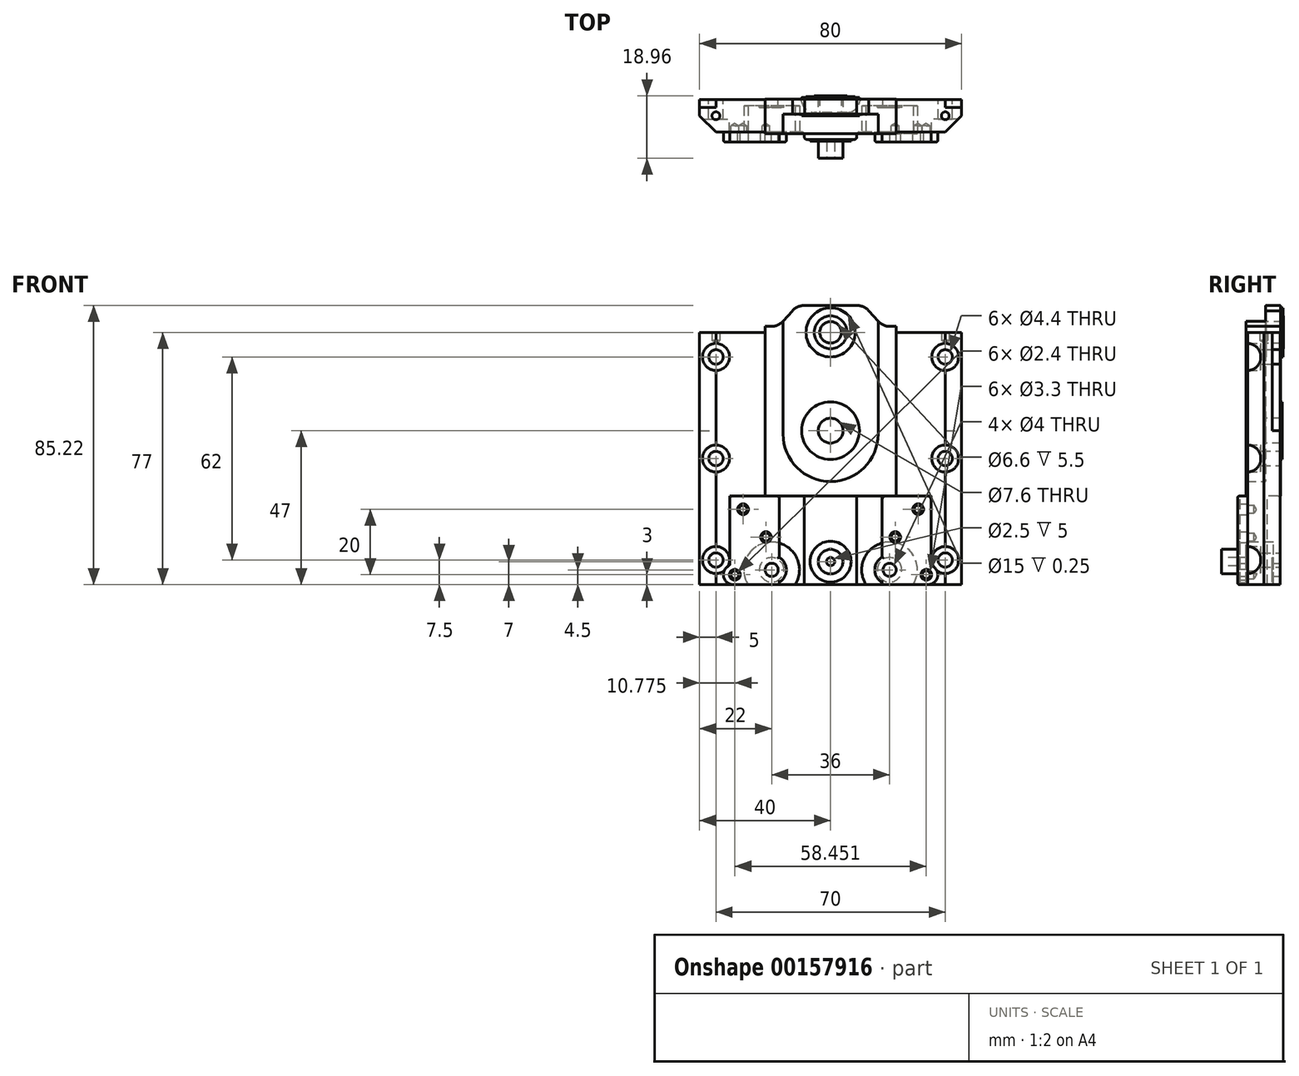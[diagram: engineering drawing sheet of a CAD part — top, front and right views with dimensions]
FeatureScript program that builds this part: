
annotation { "Feature Type Name" : "Feature", "Feature Type Description" : "" }
export const myFeature = defineFeature(function(context is Context, id is Id, definition is map)
    precondition{}
    {
        {
            var Q0;
            Q0=qCreatedBy(makeId("Front.planeOp"),FACE);
            var sketch = newSketch(context, id + "F0", { "sketchPlane" : qUnion([Q0])});
            skArc(sketch, "E0.MirrorCS", {"start": v(7.93, 38.21) * mm, "mid": v(9.99, 37.84) * mm, "end": v(11.66, 36.57) * mm});
            skArc(sketch, "E1.MirrorCS", {"start": v(18.2, 31.8) * mm, "mid": v(16.18, 32.23) * mm, "end": v(14.5, 33.43) * mm});
            skLineSegment(sketch, "E2.MirrorCS", {"start": v(20, -20) * mm, "end": v(20, 31.8) * mm});
            skLineSegment(sketch, "E3", {"start": v(20, 31.8) * mm, "end": v(18.2, 31.8) * mm});
            skLineSegment(sketch, "E4", {"start": v(11.66, 36.57) * mm, "end": v(14.5, 33.43) * mm});
            skCircle(sketch, "E5", {"center": v(0, 0) * mm, "radius": 3.8 * mm});
            skLineSegment(sketch, "E6.MirrorCS", {"start": v(-20, -20) * mm, "end": v(-20, 31.8) * mm});
            skArc(sketch, "E7.MirrorCS", {"start": v(-18.2, 31.8) * mm, "mid": v(-16.18, 32.23) * mm, "end": v(-14.5, 33.43) * mm});
            skLineSegment(sketch, "E8.MirrorCS", {"start": v(-11.66, 36.57) * mm, "end": v(-14.5, 33.43) * mm});
            skArc(sketch, "E9.MirrorCS", {"start": v(-7.93, 38.21) * mm, "mid": v(-9.99, 37.84) * mm, "end": v(-11.66, 36.57) * mm});
            skLineSegment(sketch, "E10", {"start": v(-18.2, 31.8) * mm, "end": v(-20, 31.8) * mm});
            skLineSegment(sketch, "E11", {"start": v(-20, -20) * mm, "end": v(20, -20) * mm});
            skLineSegment(sketch, "E12", {"start": v(-7.93, 38.21) * mm, "end": v(7.93, 38.21) * mm});
            skSolve(sketch);
        }
        {
            var Q0;
            Q0 = qSketchRegion(id + "F0", true);
            extrude(context, id + "F1", {"entities" : qUnion([Q0]), "oppositeDirection" : true, "depth" : 4.5 * mm});
        }
        {
            var Q0;
            Q0=makeQuery(id+"F1.opExtrude","CAP_FACE",FACE,{"disambiguationData":[OSD([sQuery(id+"F0.wireOp",EDGE,"7c40d91c-51bf-44e0-baa0-2f148f85da3b.MirrorCS"),sQuery(id+"F0.wireOp",EDGE,"E0.MirrorCS"),sQuery(id+"F0.wireOp",EDGE,"E1.MirrorCS"),sQuery(id+"F0.wireOp",EDGE,"E2.MirrorCS"),sQuery(id+"F0.wireOp",EDGE,"E3"),sQuery(id+"F0.wireOp",EDGE,"ZX2brBpr-0A55-FfDv-xvMl-bLhvxCoY3JhF"),sQuery(id+"F0.wireOp",EDGE,"E4"),sQuery(id+"F0.wireOp",EDGE,"E5"),sQuery(id+"F0.wireOp",EDGE,"f4add119-3c6b-4ee7-8744-91418914288d0.MirrorCS"),sQuery(id+"F0.wireOp",EDGE,"E6.MirrorCS"),sQuery(id+"F0.wireOp",EDGE,"E7.MirrorCS"),sQuery(id+"F0.wireOp",EDGE,"E8.MirrorCS"),sQuery(id+"F0.wireOp",EDGE,"2a2e974d-f992-448b-8597-4e99c86357490.MirrorCS"),sQuery(id+"F0.wireOp",EDGE,"E9.MirrorCS"),sQuery(id+"F0.wireOp",EDGE,"E10")])],"isStart":true});
            var sketch = newSketch(context, id + "F2", { "sketchPlane" : qUnion([Q0])});
            skPoint(sketch, "E13.orphan", {"position": v(9.9, 31.39) * mm});
            skLineSegment(sketch, "E14.0", {"start": v(20, -20) * mm, "end": v(20, 31.8) * mm});
            skLineSegment(sketch, "E15.0", {"start": v(20, -20) * mm, "end": v(-20, -20) * mm});
            skLineSegment(sketch, "E16.0", {"start": v(-20, -20) * mm, "end": v(-20, 31.8) * mm});
            skLineSegment(sketch, "E17.0", {"start": v(-18.2, 31.8) * mm, "end": v(-20, 31.8) * mm});
            skLineSegment(sketch, "E18.0", {"start": v(20, 31.8) * mm, "end": v(18.2, 31.8) * mm});
            skArc(sketch, "E19.0", {"start": v(18.2, 31.8) * mm, "mid": v(16.18, 32.23) * mm, "end": v(14.5, 33.43) * mm});
            skArc(sketch, "E20.0", {"start": v(-18.2, 31.8) * mm, "mid": v(-16.18, 32.23) * mm, "end": v(-14.5, 33.43) * mm});
            skLineSegment(sketch, "E21", {"start": v(-14.5, 33.43) * mm, "end": v(-14.5, -1.03) * mm});
            skLineSegment(sketch, "E22", {"start": v(14.5, 33.43) * mm, "end": v(14.5, -1.03) * mm});
            skArc(sketch, "E23", {"start": v(-14.5, -1.03) * mm, "mid": v(0, -15.54) * mm, "end": v(14.5, -1.03) * mm});
            skSolve(sketch);
        }
        {
            var Q0;
            Q0 = qSketchRegion(id + "F2", true);
            extrude(context, id + "F3", {"entities" : qUnion([Q0]), "operationType" : NewBodyOperationType.ADD, "depth" : 6 * mm});
        }
        {
            var Q0;
            Q0=makeQuery(id+"F3.boolean.opBoolean","MERGE",FACE,{"derivedFrom":[makeQuery(id+"F1.opExtrude","SWEPT_FACE",FACE,{"disambiguationData":[OSD([sQuery(id+"F0.wireOp",EDGE,"ZX2brBpr-0A55-FfDv-xvMl-bLhvxCoY3JhF"),sQuery(id+"F0.wireOp",EDGE,"f4add119-3c6b-4ee7-8744-91418914288d0.MirrorCS")])]}),makeQuery(id+"F3.opExtrude","SWEPT_FACE",FACE,{"disambiguationData":[OSD([sQuery(id+"F2.wireOp",EDGE,"E15.0")])]})]});
            var sketch = newSketch(context, id + "F4", { "sketchPlane" : qUnion([Q0])});
            skLineSegment(sketch, "E24.0", {"start": v(5, -0.5) * mm, "end": v(-5, -0.5) * mm});
            skPoint(sketch, "E25.visualSharp", {"position": v(10.82, 7.76) * mm});
            skPoint(sketch, "E26.visualSharp", {"position": v(-11.68, 7.76) * mm});
            skArc(sketch, "E27", {"start": v(5, -0.5) * mm, "mid": v(7.56, -1.45) * mm, "end": v(8.9, -3.83) * mm});
            skArc(sketch, "E28", {"start": v(-5, -0.5) * mm, "mid": v(-7.56, -1.45) * mm, "end": v(-8.9, -3.83) * mm});
            skLineSegment(sketch, "E29", {"start": v(-7.25, 7.76) * mm, "end": v(7.25, 7.76) * mm});
            skLineSegment(sketch, "E30", {"start": v(-8, 7) * mm, "end": v(-8, 6.3) * mm});
            skLineSegment(sketch, "E31", {"start": v(8, 7) * mm, "end": v(8, 6.3) * mm});
            skPoint(sketch, "E32.visualSharp", {"position": v(-8, 7.76) * mm});
            skArc(sketch, "E32.filletArc", {"start": v(-7.25, 7.76) * mm, "mid": v(-7.78, 7.54) * mm, "end": v(-8, 7) * mm});
            skPoint(sketch, "E33.visualSharp", {"position": v(8, 7.76) * mm});
            skArc(sketch, "E33.filletArc", {"start": v(8, 7) * mm, "mid": v(7.78, 7.54) * mm, "end": v(7.25, 7.76) * mm});
            skPoint(sketch, "E34.visualSharp", {"position": v(-8, 5.54) * mm});
            skArc(sketch, "E34.filletArc", {"start": v(-8.75, 5.54) * mm, "mid": v(-8.22, 5.76) * mm, "end": v(-8, 6.3) * mm});
            skPoint(sketch, "E35.visualSharp", {"position": v(8, 5.54) * mm});
            skArc(sketch, "E35.filletArc", {"start": v(8, 6.3) * mm, "mid": v(8.22, 5.76) * mm, "end": v(8.75, 5.54) * mm});
            skPoint(sketch, "E36.visualSharp", {"position": v(-8.96, -4.46) * mm});
            skArc(sketch, "E36.filletArc", {"start": v(-9.65, -4.46) * mm, "mid": v(-9.16, -4.28) * mm, "end": v(-8.9, -3.83) * mm});
            skPoint(sketch, "E37.visualSharp", {"position": v(8.96, -4.46) * mm});
            skArc(sketch, "E37.filletArc", {"start": v(8.9, -3.83) * mm, "mid": v(9.16, -4.28) * mm, "end": v(9.65, -4.46) * mm});
            skLineSegment(sketch, "E38", {"start": v(40, -4.46) * mm, "end": v(40, 2.2) * mm});
            skLineSegment(sketch, "E39.MirrorCS", {"start": v(-40, -4.46) * mm, "end": v(-40, 2.2) * mm});
            skLineSegment(sketch, "E40", {"start": v(-9.65, -4.46) * mm, "end": v(-40, -4.46) * mm});
            skLineSegment(sketch, "E41", {"start": v(9.65, -4.46) * mm, "end": v(40, -4.46) * mm});
            skLineSegment(sketch, "E42", {"start": v(8.75, 5.54) * mm, "end": v(26.88, 5.54) * mm});
            skLineSegment(sketch, "E43", {"start": v(-8.75, 5.54) * mm, "end": v(-26.88, 5.54) * mm});
            skLineSegment(sketch, "E44", {"start": v(26.88, 5.54) * mm, "end": v(40, 5.54) * mm});
            skLineSegment(sketch, "E45", {"start": v(40, 5.54) * mm, "end": v(40, 2.2) * mm});
            skLineSegment(sketch, "E46", {"start": v(-26.88, 5.54) * mm, "end": v(-40, 5.54) * mm});
            skLineSegment(sketch, "E47", {"start": v(-40, 5.54) * mm, "end": v(-40, 2.2) * mm});
            skSolve(sketch);
        }
        {
            var Q0;
            Q0 = qSketchRegion(id + "F4", true);
            extrude(context, id + "F5", {"entities" : qUnion([Q0]), "operationType" : NewBodyOperationType.ADD, "depth" : 27 * mm});
        }
        {
            var Q0;
            Q0=makeQuery(id+"F1.opExtrude","CAP_FACE",FACE,{"disambiguationData":[OSD([sQuery(id+"F0.wireOp",EDGE,"7c40d91c-51bf-44e0-baa0-2f148f85da3b.MirrorCS"),sQuery(id+"F0.wireOp",EDGE,"E0.MirrorCS"),sQuery(id+"F0.wireOp",EDGE,"E1.MirrorCS"),sQuery(id+"F0.wireOp",EDGE,"E2.MirrorCS"),sQuery(id+"F0.wireOp",EDGE,"E3"),sQuery(id+"F0.wireOp",EDGE,"ZX2brBpr-0A55-FfDv-xvMl-bLhvxCoY3JhF"),sQuery(id+"F0.wireOp",EDGE,"E4"),sQuery(id+"F0.wireOp",EDGE,"E5"),sQuery(id+"F0.wireOp",EDGE,"f4add119-3c6b-4ee7-8744-91418914288d0.MirrorCS"),sQuery(id+"F0.wireOp",EDGE,"E6.MirrorCS"),sQuery(id+"F0.wireOp",EDGE,"E7.MirrorCS"),sQuery(id+"F0.wireOp",EDGE,"E8.MirrorCS"),sQuery(id+"F0.wireOp",EDGE,"2a2e974d-f992-448b-8597-4e99c86357490.MirrorCS"),sQuery(id+"F0.wireOp",EDGE,"E9.MirrorCS"),sQuery(id+"F0.wireOp",EDGE,"E10")])],"isStart":true});
            var sketch = newSketch(context, id + "F6", { "sketchPlane" : qUnion([Q0])});
            skCircle(sketch, "E48.0", {"center": v(0, 0) * mm, "radius": 3.8 * mm});
            skCircle(sketch, "E49.0", {"center": v(0, 0) * mm, "radius": 8.8 * mm});
            skSolve(sketch);
        }
        {
            var Q0;
            Q0 = qSketchRegion(id + "F6", true);
            extrude(context, id + "F7", {"entities" : qUnion([Q0]), "operationType" : NewBodyOperationType.ADD, "depth" : 0.5 * mm});
        }
        {
            var Q0;
            Q0=makeQuery(id+"F1.opExtrude","CAP_FACE",FACE,{"disambiguationData":[OSD([sQuery(id+"F0.wireOp",EDGE,"7c40d91c-51bf-44e0-baa0-2f148f85da3b.MirrorCS"),sQuery(id+"F0.wireOp",EDGE,"E0.MirrorCS"),sQuery(id+"F0.wireOp",EDGE,"E1.MirrorCS"),sQuery(id+"F0.wireOp",EDGE,"E2.MirrorCS"),sQuery(id+"F0.wireOp",EDGE,"E3"),sQuery(id+"F0.wireOp",EDGE,"ZX2brBpr-0A55-FfDv-xvMl-bLhvxCoY3JhF"),sQuery(id+"F0.wireOp",EDGE,"E4"),sQuery(id+"F0.wireOp",EDGE,"E5"),sQuery(id+"F0.wireOp",EDGE,"f4add119-3c6b-4ee7-8744-91418914288d0.MirrorCS"),sQuery(id+"F0.wireOp",EDGE,"E6.MirrorCS"),sQuery(id+"F0.wireOp",EDGE,"E7.MirrorCS"),sQuery(id+"F0.wireOp",EDGE,"E8.MirrorCS"),sQuery(id+"F0.wireOp",EDGE,"2a2e974d-f992-448b-8597-4e99c86357490.MirrorCS"),sQuery(id+"F0.wireOp",EDGE,"E9.MirrorCS"),sQuery(id+"F0.wireOp",EDGE,"E10")])],"isStart":false});
            var sketch = newSketch(context, id + "F8", { "sketchPlane" : qUnion([Q0])});
            skCircle(sketch, "E50.0", {"center": v(0, 0) * mm, "radius": 3.8 * mm});
            skCircle(sketch, "E51.0", {"center": v(0, 0) * mm, "radius": 8.8 * mm});
            skSolve(sketch);
        }
        {
            var Q0;
            Q0 = qSketchRegion(id + "F8", true);
            extrude(context, id + "F9", {"entities" : qUnion([Q0]), "operationType" : NewBodyOperationType.ADD, "depth" : 0.55 * mm});
        }
        {
            var Q0;
            {var subQ0=sQuery(id+"F4.wireOp",EDGE,"E45");var subQ1=sQuery(id+"F4.wireOp",EDGE,"E38");var subQ2=sQuery(id+"F4.wireOp",EDGE,"E41");var subQ3=sQuery(id+"F4.wireOp",EDGE,"E44");var subQ4=sQuery(id+"F4.wireOp",EDGE,"E42");Q0=makeQuery(id+"F5.boolean.opBoolean","SPLIT",FACE,{"disambiguationData":[TD([makeQuery(id+"F1.opExtrude","SWEPT_FACE",FACE,{"disambiguationData":[OSD([sQuery(id+"F0.wireOp",EDGE,"E2.MirrorCS")])]})])],"derivedFrom":makeQuery(id+"F5.opExtrude","CAP_FACE",FACE,{"disambiguationData":[OSD([sQuery(id+"F4.wireOp",EDGE,"E24.0"),sQuery(id+"F4.wireOp",EDGE,"E27"),sQuery(id+"F4.wireOp",EDGE,"E28"),sQuery(id+"F4.wireOp",EDGE,"E29"),sQuery(id+"F4.wireOp",EDGE,"E30"),sQuery(id+"F4.wireOp",EDGE,"E31"),sQuery(id+"F4.wireOp",EDGE,"E32.filletArc"),sQuery(id+"F4.wireOp",EDGE,"E33.filletArc"),sQuery(id+"F4.wireOp",EDGE,"E34.filletArc"),sQuery(id+"F4.wireOp",EDGE,"E35.filletArc"),sQuery(id+"F4.wireOp",EDGE,"E36.filletArc"),sQuery(id+"F4.wireOp",EDGE,"E37.filletArc"),subQ1,sQuery(id+"F4.wireOp",EDGE,"E39.MirrorCS"),sQuery(id+"F4.wireOp",EDGE,"E40"),subQ2,subQ4,sQuery(id+"F4.wireOp",EDGE,"E43"),subQ3,subQ0,sQuery(id+"F4.wireOp",EDGE,"E46"),sQuery(id+"F4.wireOp",EDGE,"E47")])],"isStart":true})});}
            var sketch = newSketch(context, id + "F10", { "sketchPlane" : qUnion([Q0])});
            skLineSegment(sketch, "E52.0", {"start": v(20, 4.46) * mm, "end": v(40, 4.46) * mm});
            skLineSegment(sketch, "E53.0", {"start": v(40, 4.46) * mm, "end": v(40, -5.54) * mm});
            skLineSegment(sketch, "E54.0", {"start": v(20, -5.54) * mm, "end": v(40, -5.54) * mm});
            skLineSegment(sketch, "E55", {"start": v(20, 4.46) * mm, "end": v(20, -5.54) * mm});
            skLineSegment(sketch, "E56.MirrorCS", {"start": v(-20, 4.46) * mm, "end": v(-40, 4.46) * mm});
            skLineSegment(sketch, "E57.MirrorCS", {"start": v(-40, 4.46) * mm, "end": v(-40, -5.54) * mm});
            skLineSegment(sketch, "E58.MirrorCS", {"start": v(-20, -5.54) * mm, "end": v(-40, -5.54) * mm});
            skLineSegment(sketch, "E59.MirrorCS", {"start": v(-20, 4.46) * mm, "end": v(-20, -5.54) * mm});
            skSolve(sketch);
        }
        {
            var Q0;
            Q0 = qSketchRegion(id + "F10", true);
            extrude(context, id + "F11", {"entities" : qUnion([Q0]), "operationType" : NewBodyOperationType.ADD, "depth" : 50 * mm});
        }
        {
            var Q0;
            Q0=makeQuery(id+"F11.boolean.opBoolean","MERGE",EDGE,{"derivedFrom":[makeQuery(id+"F5.opExtrude","SWEPT_EDGE",EDGE,{"disambiguationData":[OSD([sQuery(id+"F4.wireOp",EDGE,"E44"),sQuery(id+"F4.wireOp",EDGE,"E45")])]}),makeQuery(id+"F11.opExtrude","SWEPT_EDGE",EDGE,{"disambiguationData":[OSD([sQuery(id+"F10.wireOp",EDGE,"E53.0"),sQuery(id+"F10.wireOp",EDGE,"E54.0")])]})]});
            var Q1;
            Q1=makeQuery(id+"F11.boolean.opBoolean","MERGE",EDGE,{"derivedFrom":[makeQuery(id+"F5.opExtrude","SWEPT_EDGE",EDGE,{"disambiguationData":[OSD([sQuery(id+"F4.wireOp",EDGE,"E46"),sQuery(id+"F4.wireOp",EDGE,"E47")])]}),makeQuery(id+"F11.opExtrude","SWEPT_EDGE",EDGE,{"disambiguationData":[OSD([sQuery(id+"F10.wireOp",EDGE,"E57.MirrorCS"),sQuery(id+"F10.wireOp",EDGE,"E58.MirrorCS")])]})]});
            chamfer(context, id + "F12", {"entities" : qUnion([Q0, Q1]), "width" : 5 * mm, "tangentPropagation" : true});
        }
        {
            var Q0;
            {var subQ0=sQuery(id+"F4.wireOp",EDGE,"E29");Q0=makeQuery(id+"F9QGCB94PZabjkV_1.boolean.opBoolean","MERGE",FACE,{"derivedFrom":[makeQuery(id+"F5.opExtrude","SWEPT_FACE",FACE,{"disambiguationData":[OSD([subQ0])]}),makeQuery(id+"F9QGCB94PZabjkV_1.opExtrude","SWEPT_FACE",FACE,{"disambiguationData":[OSD([subQ0])]})]});}
            var sketch = newSketch(context, id + "F13", { "sketchPlane" : qUnion([Q0])});
            skCircle(sketch, "E60", {"center": v(0, -40) * mm, "radius": 6.25 * mm});
            skSolve(sketch);
        }
        {
            var Q0;
            Q0 = qSketchRegion(id + "F13", true);
            extrude(context, id + "F14", {"entities" : qUnion([Q0]), "operationType" : NewBodyOperationType.ADD, "depth" : 0.5 * mm});
        }
        {
            var Q0;
            Q0=makeQuery(id+"F14.opExtrude","CAP_FACE",FACE,{"disambiguationData":[OSD([sQuery(id+"F13.wireOp",EDGE,"E60")])],"isStart":false});
            var sketch = newSketch(context, id + "F15", { "sketchPlane" : qUnion([Q0])});
            skCircle(sketch, "E61", {"center": v(0, -40) * mm, "radius": 3.75 * mm});
            skSolve(sketch);
        }
        {
            var Q0;
            Q0 = qSketchRegion(id + "F15", true);
            extrude(context, id + "F16", {"entities" : qUnion([Q0]), "operationType" : NewBodyOperationType.ADD, "depth" : 5.2 * mm});
        }
        {
            var Q0;
            Q0=makeQuery(id+"F16.opExtrude","CAP_FACE",FACE,{"disambiguationData":[OSD([sQuery(id+"F15.wireOp",EDGE,"E61")])],"isStart":false});
            var sketch = newSketch(context, id + "F17", { "sketchPlane" : qUnion([Q0])});
            skCircle(sketch, "E62", {"center": v(0, -40) * mm, "radius": 1.25 * mm});
            skSolve(sketch);
        }
        {
            var Q0;
            Q0 = qSketchRegion(id + "F17", true);
            extrude(context, id + "F18", {"entities" : qUnion([Q0]), "operationType" : NewBodyOperationType.REMOVE, "oppositeDirection" : true, "depth" : 5 * mm});
        }
        {
            var Q0;
            Q0=makeQuery(id+"F11.boolean.opBoolean","MERGE",FACE,{"derivedFrom":[makeQuery(id+"F5.opExtrude","SWEPT_FACE",FACE,{"disambiguationData":[OSD([sQuery(id+"F4.wireOp",EDGE,"E42"),sQuery(id+"F4.wireOp",EDGE,"E44")])]}),makeQuery(id+"F11.opExtrude","SWEPT_FACE",FACE,{"disambiguationData":[OSD([sQuery(id+"F10.wireOp",EDGE,"E54.0")])]})]});
            var sketch = newSketch(context, id + "F19", { "sketchPlane" : qUnion([Q0])});
            skCircle(sketch, "E63", {"center": v(18, -42.5) * mm, "radius": 8.5 * mm});
            skCircle(sketch, "E64.MirrorC", {"center": v(-18, -42.5) * mm, "radius": 8.5 * mm});
            skSolve(sketch);
        }
        {
            var Q0;
            Q0 = qSketchRegion(id + "F19", true);
            extrude(context, id + "F20", {"entities" : qUnion([Q0]), "operationType" : NewBodyOperationType.REMOVE, "oppositeDirection" : true, "depth" : 8 * mm});
        }
        {
            var Q0;
            Q0=makeQuery(id+"F20.boolean.opBoolean","COPY",FACE,{"derivedFrom":makeQuery(id+"F20.opExtrude","CAP_FACE",FACE,{"disambiguationData":[OSD([sQuery(id+"F19.wireOp",EDGE,"E63")])],"isStart":false})});
            var sketch = newSketch(context, id + "F21", { "sketchPlane" : qUnion([Q0])});
            skCircle(sketch, "E65", {"center": v(18, -42.5) * mm, "radius": 2 * mm});
            skCircle(sketch, "E66", {"center": v(18, -42.5) * mm, "radius": 3.75 * mm});
            skCircle(sketch, "E67.MirrorC", {"center": v(-18, -42.5) * mm, "radius": 2 * mm});
            skCircle(sketch, "E68.MirrorC", {"center": v(-18, -42.5) * mm, "radius": 3.75 * mm});
            skSolve(sketch);
        }
        {
            var Q0;
            Q0 = qSketchRegion(id + "F21", true);
            extrude(context, id + "F22", {"entities" : qUnion([Q0]), "operationType" : NewBodyOperationType.ADD, "depth" : 0.5 * mm});
        }
        {
            var Q0;
            Q0=makeQuery(id+"F22.boolean.opBoolean","SPLIT",FACE,{"disambiguationData":[TD([makeQuery(id+"F22.opExtrude","SWEPT_FACE",FACE,{"disambiguationData":[OSD([sQuery(id+"F21.wireOp",EDGE,"E65")])]})])],"derivedFrom":makeQuery(id+"F20.boolean.opBoolean","COPY",FACE,{"derivedFrom":makeQuery(id+"F20.opExtrude","CAP_FACE",FACE,{"disambiguationData":[OSD([sQuery(id+"F19.wireOp",EDGE,"E63")])],"isStart":false})})});
            var Q1;
            Q1=makeQuery(id+"F22.boolean.opBoolean","SPLIT",FACE,{"disambiguationData":[TD([makeQuery(id+"F22.opExtrude","SWEPT_FACE",FACE,{"disambiguationData":[OSD([sQuery(id+"F21.wireOp",EDGE,"E67.MirrorC")])]})])],"derivedFrom":makeQuery(id+"F20.boolean.opBoolean","COPY",FACE,{"derivedFrom":makeQuery(id+"F20.opExtrude","CAP_FACE",FACE,{"disambiguationData":[OSD([sQuery(id+"F19.wireOp",EDGE,"E64.MirrorC")])],"isStart":false})})});
            extrude(context, id + "F23", {"entities" : qUnion([Q0, Q1]), "operationType" : NewBodyOperationType.REMOVE, "oppositeDirection" : true, "depth" : 5 * mm});
        }
        {
            var Q0;
            {var subQ0=sQuery(id+"F4.wireOp",EDGE,"E35.filletArc");var subQ1=sQuery(id+"F19.wireOp",EDGE,"E63");var subQ2=sQuery(id+"F10.wireOp",EDGE,"E54.0");var subQ3=sQuery(id+"F10.wireOp",EDGE,"E53.0");var subQ4=sQuery(id+"F4.wireOp",EDGE,"E44");Q0=makeQuery(id+"F20.boolean.opBoolean","SPLIT",FACE,{"disambiguationData":[TD([makeQuery(id+"F1.opExtrude","SWEPT_FACE",FACE,{"disambiguationData":[OSD([sQuery(id+"F0.wireOp",EDGE,"E2.MirrorCS")])]}),makeQuery(id+"F1.opExtrude","SWEPT_FACE",FACE,{"disambiguationData":[OSD([sQuery(id+"F0.wireOp",EDGE,"ZX2brBpr-0A55-FfDv-xvMl-bLhvxCoY3JhF"),sQuery(id+"F0.wireOp",EDGE,"f4add119-3c6b-4ee7-8744-91418914288d0.MirrorCS")])]}),makeQuery(id+"F3.opExtrude","SWEPT_FACE",FACE,{"disambiguationData":[OSD([sQuery(id+"F2.wireOp",EDGE,"E14.0")])]}),makeQuery(id+"F3.opExtrude","SWEPT_FACE",FACE,{"disambiguationData":[OSD([sQuery(id+"F2.wireOp",EDGE,"E15.0")])]}),makeQuery(id+"F5.opExtrude","SWEPT_FACE",FACE,{"disambiguationData":[OSD([subQ0])]}),makeQuery(id+"F9QGCB94PZabjkV_1.opExtrude","SWEPT_FACE",FACE,{"disambiguationData":[OSD([subQ0])]}),makeQuery(id+"F11.opExtrude","CAP_FACE",FACE,{"disambiguationData":[OSD([sQuery(id+"F10.wireOp",EDGE,"E52.0"),subQ3,subQ2,sQuery(id+"F10.wireOp",EDGE,"E55")])],"isStart":false}),makeQuery(id+"F12.opChamfer","BLEND_FACE",FACE,{"disambiguationData":[OSD([subQ4,sQuery(id+"F4.wireOp",EDGE,"E45"),subQ3,subQ2])]}),makeQuery(id+"F20.opExtrude","SWEPT_FACE",FACE,{"disambiguationData":[OSD([subQ1])]}),makeQuery(id+"F20.opExtrude","CAP_FACE",FACE,{"disambiguationData":[OSD([subQ1])],"isStart":true})])],"derivedFrom":makeQuery(id+"F11.boolean.opBoolean","MERGE",FACE,{"derivedFrom":[makeQuery(id+"F5.opExtrude","SWEPT_FACE",FACE,{"disambiguationData":[OSD([sQuery(id+"F4.wireOp",EDGE,"E42"),subQ4])]}),makeQuery(id+"F11.opExtrude","SWEPT_FACE",FACE,{"disambiguationData":[OSD([subQ2])]})]})});}
            var sketch = newSketch(context, id + "F24", { "sketchPlane" : qUnion([Q0])});
            skCircle(sketch, "E69.0", {"center": v(18, -42.5) * mm, "radius": 3.75 * mm});
            skCircle(sketch, "E70", {"center": v(18, -42.5) * mm, "radius": 8.5 * mm});
            skCircle(sketch, "E71.MirrorC", {"center": v(-18, -42.5) * mm, "radius": 8.5 * mm});
            skCircle(sketch, "E72.MirrorC", {"center": v(-18, -42.5) * mm, "radius": 3.75 * mm});
            skSolve(sketch);
        }
        {
            var Q0;
            Q0=makeQuery(id+"F7.opExtrude","CAP_EDGE",EDGE,{"disambiguationData":[OSD([sQuery(id+"F6.wireOp",EDGE,"E48.0")])],"isStart":false});
            fillet(context, id + "F25", {"entities" : qUnion([Q0]), "radius" : 0.5 * mm, "tangentPropagation" : true, "allowEdgeOverflow" : false});
        }
        {
            var Q0;
            {var subQ0=sQuery(id+"F19.wireOp",EDGE,"E64.MirrorC");var subQ1=sQuery(id+"F4.wireOp",EDGE,"E47");var subQ2=sQuery(id+"F4.wireOp",EDGE,"E46");var subQ3=sQuery(id+"F4.wireOp",EDGE,"E43");var subQ4=sQuery(id+"F4.wireOp",EDGE,"E34.filletArc");var subQ5=sQuery(id+"F10.wireOp",EDGE,"E58.MirrorCS");var subQ6=sQuery(id+"F10.wireOp",EDGE,"E57.MirrorCS");Q0=makeQuery(id+"F20.boolean.opBoolean","SPLIT",FACE,{"disambiguationData":[TD([makeQuery(id+"F1.opExtrude","SWEPT_FACE",FACE,{"disambiguationData":[OSD([sQuery(id+"F0.wireOp",EDGE,"E6.MirrorCS")])]}),makeQuery(id+"F1.opExtrude","SWEPT_FACE",FACE,{"disambiguationData":[OSD([sQuery(id+"F0.wireOp",EDGE,"E11")])]}),makeQuery(id+"F3.opExtrude","SWEPT_FACE",FACE,{"disambiguationData":[OSD([sQuery(id+"F2.wireOp",EDGE,"E15.0")])]}),makeQuery(id+"F3.opExtrude","SWEPT_FACE",FACE,{"disambiguationData":[OSD([sQuery(id+"F2.wireOp",EDGE,"E16.0")])]}),makeQuery(id+"F5.opExtrude","CAP_FACE",FACE,{"disambiguationData":[OSD([sQuery(id+"F4.wireOp",EDGE,"E24.0"),sQuery(id+"F4.wireOp",EDGE,"E27"),sQuery(id+"F4.wireOp",EDGE,"E28"),sQuery(id+"F4.wireOp",EDGE,"E29"),sQuery(id+"F4.wireOp",EDGE,"E30"),sQuery(id+"F4.wireOp",EDGE,"E31"),sQuery(id+"F4.wireOp",EDGE,"E32.filletArc"),sQuery(id+"F4.wireOp",EDGE,"E33.filletArc"),subQ4,sQuery(id+"F4.wireOp",EDGE,"E35.filletArc"),sQuery(id+"F4.wireOp",EDGE,"E36.filletArc"),sQuery(id+"F4.wireOp",EDGE,"E37.filletArc"),sQuery(id+"F4.wireOp",EDGE,"E38"),sQuery(id+"F4.wireOp",EDGE,"E39.MirrorCS"),sQuery(id+"F4.wireOp",EDGE,"E40"),sQuery(id+"F4.wireOp",EDGE,"E41"),sQuery(id+"F4.wireOp",EDGE,"E42"),subQ3,sQuery(id+"F4.wireOp",EDGE,"E44"),sQuery(id+"F4.wireOp",EDGE,"E45"),subQ2,subQ1])],"isStart":false}),makeQuery(id+"F5.opExtrude","SWEPT_FACE",FACE,{"disambiguationData":[OSD([subQ4])]}),makeQuery(id+"F11.opExtrude","CAP_FACE",FACE,{"disambiguationData":[OSD([sQuery(id+"F10.wireOp",EDGE,"E56.MirrorCS"),subQ6,subQ5,sQuery(id+"F10.wireOp",EDGE,"E59.MirrorCS")])],"isStart":false}),makeQuery(id+"F12.opChamfer","BLEND_FACE",FACE,{"disambiguationData":[OSD([subQ2,subQ1,subQ6,subQ5])]}),makeQuery(id+"F20.opExtrude","SWEPT_FACE",FACE,{"disambiguationData":[OSD([subQ0])]}),makeQuery(id+"F20.opExtrude","CAP_FACE",FACE,{"disambiguationData":[OSD([subQ0])],"isStart":true})])],"derivedFrom":makeQuery(id+"F11.boolean.opBoolean","MERGE",FACE,{"derivedFrom":[makeQuery(id+"F5.opExtrude","SWEPT_FACE",FACE,{"disambiguationData":[OSD([subQ3,subQ2])]}),makeQuery(id+"F11.opExtrude","SWEPT_FACE",FACE,{"disambiguationData":[OSD([subQ5])]})]})});}
            var sketch = newSketch(context, id + "F26", { "sketchPlane" : qUnion([Q0])});
            skCircle(sketch, "E73", {"center": v(-35, -39.5) * mm, "radius": 2.1 * mm});
            skCircle(sketch, "E74", {"center": v(-35, 22.5) * mm, "radius": 2.3 * mm});
            skCircle(sketch, "E75", {"center": v(-35, -8.5) * mm, "radius": 2 * mm});
            skCircle(sketch, "E76.MirrorC", {"center": v(35, 22.5) * mm, "radius": 2.3 * mm});
            skCircle(sketch, "E77.MirrorC", {"center": v(35, -8.5) * mm, "radius": 2 * mm});
            skCircle(sketch, "E78.MirrorC", {"center": v(35, -39.5) * mm, "radius": 2.1 * mm});
            skSolve(sketch);
        }
        {
            var Q0;
            Q0=sQuery(id+"F26.wireOp",VERTEX,"E74.center");
            var Q1;
            Q1=sQuery(id+"F26.wireOp",VERTEX,"E75.center");
            var Q2;
            Q2=sQuery(id+"F26.wireOp",VERTEX,"E73.center");
            var Q3;
            Q3=sQuery(id+"F26.wireOp",VERTEX,"E78.MirrorC.center");
            var Q4;
            Q4=sQuery(id+"F26.wireOp",VERTEX,"E77.MirrorC.center");
            var Q5;
            Q5=sQuery(id+"F26.wireOp",VERTEX,"E76.MirrorC.center");
            var Q6;
            Q6=makeQuery(id+"F1.opExtrude","SWEPT_BODY",BODY,{"disambiguationData":[OSD([sQuery(id+"F0.wireOp",EDGE,"7c40d91c-51bf-44e0-baa0-2f148f85da3b.MirrorCS"),sQuery(id+"F0.wireOp",EDGE,"E0.MirrorCS"),sQuery(id+"F0.wireOp",EDGE,"E1.MirrorCS"),sQuery(id+"F0.wireOp",EDGE,"E2.MirrorCS"),sQuery(id+"F0.wireOp",EDGE,"E3"),sQuery(id+"F0.wireOp",EDGE,"E4"),sQuery(id+"F0.wireOp",EDGE,"E5"),sQuery(id+"F0.wireOp",EDGE,"E6.MirrorCS"),sQuery(id+"F0.wireOp",EDGE,"E7.MirrorCS"),sQuery(id+"F0.wireOp",EDGE,"E8.MirrorCS"),sQuery(id+"F0.wireOp",EDGE,"2a2e974d-f992-448b-8597-4e99c86357490.MirrorCS"),sQuery(id+"F0.wireOp",EDGE,"E9.MirrorCS"),sQuery(id+"F0.wireOp",EDGE,"E10"),sQuery(id+"F0.wireOp",EDGE,"E11")])]});
            hole(context, id + "F27", {"style" : HoleStyle.C_BORE, "endStyle" : HoleEndStyle.THROUGH, "standardTappedOrClearance" : lookupTablePath({ "standard" : "ISO", "fit" : "Normal", "size" : "M4", "type" : "Clearance" }), "standardBlindInLast" : lookupTablePath({ "fit" : "Standard", "standard" : "ISO", "size" : "M4", "type" : "Clearance" }), "holeDiameter" : 4.4 * mm, "cBoreDiameter" : 8.25 * mm, "cBoreDepth" : 4 * mm, "locations" : qUnion([Q0, Q1, Q2, Q3, Q4, Q5]), "scope" : qUnion([Q6]), "isTappedThrough" : true, "startStyle" : HoleStartStyle.SKETCH});
        }
        {
            var Q0;
            Q0=makeQuery(id+"F11.boolean.opBoolean","MERGE",FACE,{"derivedFrom":[makeQuery(id+"F5.opExtrude","SWEPT_FACE",FACE,{"disambiguationData":[OSD([sQuery(id+"F4.wireOp",EDGE,"E42"),sQuery(id+"F4.wireOp",EDGE,"E44")])]}),makeQuery(id+"F11.opExtrude","SWEPT_FACE",FACE,{"disambiguationData":[OSD([sQuery(id+"F10.wireOp",EDGE,"E54.0")])]})]});
            var sketch = newSketch(context, id + "F28", { "sketchPlane" : qUnion([Q0])});
            skLineSegment(sketch, "E79", {"start": v(15.73, -20) * mm, "end": v(30.73, -20) * mm});
            skCircle(sketch, "E80.0", {"center": v(18, -42.5) * mm, "radius": 2 * mm});
            skCircle(sketch, "E81.MirrorC", {"center": v(-18, -42.5) * mm, "radius": 2 * mm});
            skLineSegment(sketch, "E82", {"start": v(30.73, -20) * mm, "end": v(30.73, -40.54) * mm});
            skLineSegment(sketch, "E83", {"start": v(29.73, -47) * mm, "end": v(15.73, -47) * mm});
            skLineSegment(sketch, "E84", {"start": v(15.73, -47) * mm, "end": v(15.73, -46.38) * mm});
            skPoint(sketch, "E85.orphan", {"position": v(8.75, -20) * mm});
            skArc(sketch, "E86", {"start": v(15.73, -38.62) * mm, "mid": v(13.5, -42.5) * mm, "end": v(15.73, -46.38) * mm});
            skLineSegment(sketch, "E87.trimOffspring", {"start": v(15.73, -38.62) * mm, "end": v(15.73, -20) * mm});
            skLineSegment(sketch, "E88.MirrorCS", {"start": v(-30.73, -20) * mm, "end": v(-30.73, -40.54) * mm});
            skLineSegment(sketch, "E89.MirrorCS", {"start": v(-29.73, -47) * mm, "end": v(-15.73, -47) * mm});
            skArc(sketch, "E90.MirrorCS", {"start": v(-15.73, -38.62) * mm, "mid": v(-13.5, -42.5) * mm, "end": v(-15.73, -46.38) * mm});
            skLineSegment(sketch, "E91.MirrorCS", {"start": v(-15.73, -38.62) * mm, "end": v(-15.73, -20) * mm});
            skLineSegment(sketch, "E92.MirrorCS", {"start": v(-15.73, -20) * mm, "end": v(-30.73, -20) * mm});
            skLineSegment(sketch, "E93", {"start": v(-15.73, -46.38) * mm, "end": v(-15.73, -47) * mm});
            skArc(sketch, "E94", {"start": v(29.73, -47) * mm, "mid": v(32.62, -44.78) * mm, "end": v(31.23, -41.4) * mm});
            skArc(sketch, "E95.MirrorC", {"start": v(-29.73, -47) * mm, "mid": v(-32.62, -44.78) * mm, "end": v(-31.23, -41.4) * mm});
            skPoint(sketch, "E96.orphan", {"position": v(30.73, -47) * mm});
            skPoint(sketch, "E97.visualSharp", {"position": v(30.73, -41.17) * mm});
            skArc(sketch, "E97.filletArc", {"start": v(30.73, -40.54) * mm, "mid": v(30.86, -41.04) * mm, "end": v(31.23, -41.4) * mm});
            skPoint(sketch, "E98.trimOffspring.end.orphan", {"position": v(-30.73, -47) * mm});
            skPoint(sketch, "E99.visualSharp", {"position": v(-30.73, -41.17) * mm});
            skArc(sketch, "E99.filletArc", {"start": v(-31.23, -41.4) * mm, "mid": v(-30.86, -41.04) * mm, "end": v(-30.73, -40.54) * mm});
            skSolve(sketch);
        }
        {
            var Q0;
            Q0 = qSketchRegion(id + "F28", true);
            extrude(context, id + "F29", {"entities" : qUnion([Q0]), "depth" : 3 * mm});
        }
        {
            var Q0;
            Q0=makeQuery(id+"F24.imprint","IMPRINT",FACE,{"disambiguationData":[TD([[makeQuery(id+"F24.imprint","IMPRINT",EDGE,{"derivedFrom":sQuery(id+"F24.wireOp",EDGE,"E71.MirrorC")}),-1.0]])]});
            var Q1;
            Q1=makeQuery(id+"F24.imprint","IMPRINT",FACE,{"disambiguationData":[TD([[makeQuery(id+"F24.imprint","IMPRINT",EDGE,{"derivedFrom":sQuery(id+"F24.wireOp",EDGE,"E69.0")}),-1.0]])]});
            extrude(context, id + "F30", {"entities" : qUnion([Q0, Q1]), "operationType" : NewBodyOperationType.REMOVE, "depth" : 0.5 * mm});
        }
        {
            var Q0;
            Q0=makeQuery(id+"F29.opExtrude","CAP_EDGE",EDGE,{"disambiguationData":[OSD([sQuery(id+"F28.wireOp",EDGE,"E92.MirrorCS")])],"isStart":false});
            var Q1;
            Q1=makeQuery(id+"F29.opExtrude","CAP_EDGE",EDGE,{"disambiguationData":[OSD([sQuery(id+"F28.wireOp",EDGE,"E88.MirrorCS")])],"isStart":false});
            var Q2;
            Q2=makeQuery(id+"F29.opExtrude","CAP_EDGE",EDGE,{"disambiguationData":[OSD([sQuery(id+"F28.wireOp",EDGE,"E89.MirrorCS")])],"isStart":false});
            var Q3;
            Q3=makeQuery(id+"F29.opExtrude","CAP_EDGE",EDGE,{"disambiguationData":[OSD([sQuery(id+"F28.wireOp",EDGE,"E79")])],"isStart":false});
            var Q4;
            Q4=makeQuery(id+"F29.opExtrude","CAP_EDGE",EDGE,{"disambiguationData":[OSD([sQuery(id+"F28.wireOp",EDGE,"E82")])],"isStart":false});
            var Q5;
            Q5=makeQuery(id+"F29.opExtrude","CAP_EDGE",EDGE,{"disambiguationData":[OSD([sQuery(id+"F28.wireOp",EDGE,"E83")])],"isStart":false});
            var Q6;
            Q6=makeQuery(id+"F29.opExtrude","CAP_EDGE",EDGE,{"disambiguationData":[OSD([sQuery(id+"F28.wireOp",EDGE,"E87.trimOffspring")])],"isStart":false});
            var Q7;
            Q7=makeQuery(id+"F29.opExtrude","CAP_EDGE",EDGE,{"disambiguationData":[OSD([sQuery(id+"F28.wireOp",EDGE,"E91.MirrorCS")])],"isStart":false});
            var Q8;
            Q8=makeQuery(id+"F29.opExtrude","CAP_EDGE",EDGE,{"disambiguationData":[OSD([sQuery(id+"F28.wireOp",EDGE,"E90.MirrorCS")])],"isStart":false});
            var Q9;
            Q9=makeQuery(id+"F29.opExtrude","CAP_EDGE",EDGE,{"disambiguationData":[OSD([sQuery(id+"F28.wireOp",EDGE,"E86")])],"isStart":false});
            fillet(context, id + "F31", {"entities" : qUnion([Q0, Q1, Q2, Q3, Q4, Q5, Q6, Q7, Q8, Q9]), "radius" : 0.5 * mm, "tangentPropagation" : true, "allowEdgeOverflow" : false});
        }
        {
            var Q0;
            Q0=makeQuery(id+"F29.opExtrude","CAP_FACE",FACE,{"disambiguationData":[OSD([sQuery(id+"F28.wireOp",EDGE,"E79"),sQuery(id+"F28.wireOp",EDGE,"E80.0"),sQuery(id+"F28.wireOp",EDGE,"E82"),sQuery(id+"F28.wireOp",EDGE,"E83"),sQuery(id+"F28.wireOp",EDGE,"E84"),sQuery(id+"F28.wireOp",EDGE,"E86"),sQuery(id+"F28.wireOp",EDGE,"E87.trimOffspring")])],"isStart":false});
            var sketch = newSketch(context, id + "F32", { "sketchPlane" : qUnion([Q0])});
            skCircle(sketch, "E100", {"center": v(26.73, -24) * mm, "radius": 2 * mm});
            skCircle(sketch, "E101", {"center": v(29.23, -44) * mm, "radius": 2 * mm});
            skCircle(sketch, "E102", {"center": v(19.73, -32.5) * mm, "radius": 1.64 * mm});
            skCircle(sketch, "E103.MirrorC", {"center": v(-26.73, -24) * mm, "radius": 2 * mm});
            skCircle(sketch, "E104.MirrorC", {"center": v(-29.23, -44) * mm, "radius": 2 * mm});
            skCircle(sketch, "E105.MirrorC", {"center": v(-19.73, -32.5) * mm, "radius": 1.64 * mm});
            skSolve(sketch);
        }
        {
            var Q0;
            Q0=sQuery(id+"F32.wireOp",VERTEX,"E100.center");
            var Q1;
            Q1=sQuery(id+"F32.wireOp",VERTEX,"E102.center");
            var Q2;
            Q2=sQuery(id+"F32.wireOp",VERTEX,"E101.center");
            var Q3;
            Q3=sQuery(id+"F32.wireOp",VERTEX,"E105.MirrorC.center");
            var Q4;
            Q4=sQuery(id+"F32.wireOp",VERTEX,"E103.MirrorC.center");
            var Q5;
            Q5=sQuery(id+"F32.wireOp",VERTEX,"E104.MirrorC.center");
            var Q6;
            Q6=makeQuery(id+"F29.opExtrude","SWEPT_BODY",BODY,{"disambiguationData":[OSD([sQuery(id+"F28.wireOp",EDGE,"E79"),sQuery(id+"F28.wireOp",EDGE,"E80.0"),sQuery(id+"F28.wireOp",EDGE,"E82"),sQuery(id+"F28.wireOp",EDGE,"E83"),sQuery(id+"F28.wireOp",EDGE,"E84"),sQuery(id+"F28.wireOp",EDGE,"E86"),sQuery(id+"F28.wireOp",EDGE,"E87.trimOffspring")])]});
            var Q7;
            Q7=makeQuery(id+"F29.opExtrude","SWEPT_BODY",BODY,{"disambiguationData":[OSD([sQuery(id+"F28.wireOp",EDGE,"E81.MirrorC"),sQuery(id+"F28.wireOp",EDGE,"E88.MirrorCS"),sQuery(id+"F28.wireOp",EDGE,"E89.MirrorCS"),sQuery(id+"F28.wireOp",EDGE,"E90.MirrorCS"),sQuery(id+"F28.wireOp",EDGE,"E91.MirrorCS"),sQuery(id+"F28.wireOp",EDGE,"E92.MirrorCS"),sQuery(id+"F28.wireOp",EDGE,"E93")])]});
            hole(context, id + "F33", {"style" : HoleStyle.SIMPLE, "endStyle" : HoleEndStyle.THROUGH, "standardTappedOrClearance" : lookupTablePath({ "standard" : "ISO", "fit" : "Normal", "size" : "M3", "type" : "Clearance" }), "standardBlindInLast" : lookupTablePath({ "fit" : "Standard", "standard" : "ISO", "size" : "M3", "type" : "Clearance" }), "holeDiameter" : 3.3 * mm, "locations" : qUnion([Q0, Q1, Q2, Q3, Q4, Q5]), "scope" : qUnion([Q6, Q7]), "isTappedThrough" : true, "startStyle" : HoleStartStyle.SKETCH});
        }
        {
            var Q0;
            Q0=sQuery(id+"F32.wireOp",VERTEX,"E100.center");
            var Q1;
            Q1=sQuery(id+"F32.wireOp",VERTEX,"E101.center");
            var Q2;
            Q2=sQuery(id+"F32.wireOp",VERTEX,"E102.center");
            var Q3;
            Q3=sQuery(id+"F32.wireOp",VERTEX,"E105.MirrorC.center");
            var Q4;
            Q4=sQuery(id+"F32.wireOp",VERTEX,"E103.MirrorC.center");
            var Q5;
            Q5=sQuery(id+"F32.wireOp",VERTEX,"E104.MirrorC.center");
            var Q6;
            Q6=makeQuery(id+"F1.opExtrude","SWEPT_BODY",BODY,{"disambiguationData":[OSD([sQuery(id+"F0.wireOp",EDGE,"7c40d91c-51bf-44e0-baa0-2f148f85da3b.MirrorCS"),sQuery(id+"F0.wireOp",EDGE,"E0.MirrorCS"),sQuery(id+"F0.wireOp",EDGE,"E1.MirrorCS"),sQuery(id+"F0.wireOp",EDGE,"E2.MirrorCS"),sQuery(id+"F0.wireOp",EDGE,"E3"),sQuery(id+"F0.wireOp",EDGE,"E4"),sQuery(id+"F0.wireOp",EDGE,"E5"),sQuery(id+"F0.wireOp",EDGE,"E6.MirrorCS"),sQuery(id+"F0.wireOp",EDGE,"E7.MirrorCS"),sQuery(id+"F0.wireOp",EDGE,"E8.MirrorCS"),sQuery(id+"F0.wireOp",EDGE,"2a2e974d-f992-448b-8597-4e99c86357490.MirrorCS"),sQuery(id+"F0.wireOp",EDGE,"E9.MirrorCS"),sQuery(id+"F0.wireOp",EDGE,"E10"),sQuery(id+"F0.wireOp",EDGE,"E11")])]});
            hole(context, id + "F34", {"style" : HoleStyle.SIMPLE, "endStyle" : HoleEndStyle.BLIND, "standardTappedOrClearance" : lookupTablePath({ "standard" : "ISO", "engagement" : "75%", "pitch" : "0.6 mm", "size" : "M3", "type" : "Tapped" }), "standardBlindInLast" : lookupTablePath({ "standard" : "ISO", "engagement" : "75%", "pitch" : "0.6 mm", "size" : "M3", "type" : "Tapped" }), "holeDiameter" : 2.4 * mm, "holeDepth" : 5 * mm, "locations" : qUnion([Q0, Q1, Q2, Q3, Q4, Q5]), "scope" : qUnion([Q6]), "startStyle" : HoleStartStyle.SKETCH});
        }
        {
            var Q0;
            Q0=makeQuery(id+"F11.opExtrude","CAP_FACE",FACE,{"disambiguationData":[OSD([sQuery(id+"F10.wireOp",EDGE,"E52.0"),sQuery(id+"F10.wireOp",EDGE,"E53.0"),sQuery(id+"F10.wireOp",EDGE,"E54.0"),sQuery(id+"F10.wireOp",EDGE,"E55")])],"isStart":false});
            var sketch = newSketch(context, id + "F35", { "sketchPlane" : qUnion([Q0])});
            skLineSegment(sketch, "E106.bottom", {"start": v(40, 4.46) * mm, "end": v(35, 4.46) * mm});
            skLineSegment(sketch, "E106.top", {"start": v(40, 1.96) * mm, "end": v(35, 1.96) * mm});
            skLineSegment(sketch, "E106.left", {"start": v(40, 4.46) * mm, "end": v(40, 1.96) * mm});
            skLineSegment(sketch, "E106.right", {"start": v(35, 4.46) * mm, "end": v(35, 1.96) * mm});
            skLineSegment(sketch, "E107.MirrorCS", {"start": v(-40, 1.96) * mm, "end": v(-35, 1.96) * mm});
            skLineSegment(sketch, "E108.MirrorCS", {"start": v(-35, 4.46) * mm, "end": v(-35, 1.96) * mm});
            skLineSegment(sketch, "E109.MirrorCS", {"start": v(-40, 4.46) * mm, "end": v(-35, 4.46) * mm});
            skLineSegment(sketch, "E110.MirrorCS", {"start": v(-40, 4.46) * mm, "end": v(-40, 1.96) * mm});
            skSolve(sketch);
        }
        {
            var Q0;
            Q0 = qSketchRegion(id + "F35", true);
            extrude(context, id + "F36", {"entities" : qUnion([Q0]), "operationType" : NewBodyOperationType.REMOVE, "oppositeDirection" : true, "depth" : 30 * mm});
        }
        {
            var Q0;
            Q0=makeQuery(id+"F1.opExtrude","CAP_FACE",FACE,{"disambiguationData":[OSD([sQuery(id+"F0.wireOp",EDGE,"7c40d91c-51bf-44e0-baa0-2f148f85da3b.MirrorCS"),sQuery(id+"F0.wireOp",EDGE,"E0.MirrorCS"),sQuery(id+"F0.wireOp",EDGE,"E1.MirrorCS"),sQuery(id+"F0.wireOp",EDGE,"E2.MirrorCS"),sQuery(id+"F0.wireOp",EDGE,"E3"),sQuery(id+"F0.wireOp",EDGE,"E4"),sQuery(id+"F0.wireOp",EDGE,"E5"),sQuery(id+"F0.wireOp",EDGE,"E6.MirrorCS"),sQuery(id+"F0.wireOp",EDGE,"E7.MirrorCS"),sQuery(id+"F0.wireOp",EDGE,"E8.MirrorCS"),sQuery(id+"F0.wireOp",EDGE,"2a2e974d-f992-448b-8597-4e99c86357490.MirrorCS"),sQuery(id+"F0.wireOp",EDGE,"E9.MirrorCS"),sQuery(id+"F0.wireOp",EDGE,"E10"),sQuery(id+"F0.wireOp",EDGE,"E11")])],"isStart":true});
            var sketch = newSketch(context, id + "F37", { "sketchPlane" : qUnion([Q0])});
            skCircle(sketch, "E111", {"center": v(0, 30) * mm, "radius": 3.3 * mm});
            skSolve(sketch);
        }
        {
            var Q0;
            Q0 = qSketchRegion(id + "F37", true);
            extrude(context, id + "F38", {"entities" : qUnion([Q0]), "operationType" : NewBodyOperationType.REMOVE, "endBound" : BoundingType.THROUGH_ALL, "oppositeDirection" : true, "depth" : 25 * mm});
        }
        {
            var Q0;
            Q0=qCreatedBy(makeId("Front.planeOp"),FACE);
            var sketch = newSketch(context, id + "F39", { "sketchPlane" : qUnion([Q0])});
            skCircle(sketch, "E112.0", {"center": v(0, 30) * mm, "radius": 3.3 * mm});
            skCircle(sketch, "E113", {"center": v(0, 30) * mm, "radius": 7.5 * mm});
            skSolve(sketch);
        }
        {
            var Q0;
            Q0 = qSketchRegion(id + "F39", true);
            extrude(context, id + "F40", {"entities" : qUnion([Q0]), "operationType" : NewBodyOperationType.REMOVE, "oppositeDirection" : true, "depth" : 0.25 * mm});
        }
        {
            var Q0;
            Q0=makeQuery(id+"F1.opExtrude","CAP_FACE",FACE,{"disambiguationData":[OSD([sQuery(id+"F0.wireOp",EDGE,"7c40d91c-51bf-44e0-baa0-2f148f85da3b.MirrorCS"),sQuery(id+"F0.wireOp",EDGE,"E0.MirrorCS"),sQuery(id+"F0.wireOp",EDGE,"E1.MirrorCS"),sQuery(id+"F0.wireOp",EDGE,"E2.MirrorCS"),sQuery(id+"F0.wireOp",EDGE,"E3"),sQuery(id+"F0.wireOp",EDGE,"E4"),sQuery(id+"F0.wireOp",EDGE,"E5"),sQuery(id+"F0.wireOp",EDGE,"E6.MirrorCS"),sQuery(id+"F0.wireOp",EDGE,"E7.MirrorCS"),sQuery(id+"F0.wireOp",EDGE,"E8.MirrorCS"),sQuery(id+"F0.wireOp",EDGE,"2a2e974d-f992-448b-8597-4e99c86357490.MirrorCS"),sQuery(id+"F0.wireOp",EDGE,"E9.MirrorCS"),sQuery(id+"F0.wireOp",EDGE,"E10"),sQuery(id+"F0.wireOp",EDGE,"E11")])],"isStart":false});
            var sketch = newSketch(context, id + "F41", { "sketchPlane" : qUnion([Q0])});
            skCircle(sketch, "E114.0", {"center": v(0, 30) * mm, "radius": 3.3 * mm});
            skCircle(sketch, "E115", {"center": v(0, 30) * mm, "radius": 7.5 * mm});
            skSolve(sketch);
        }
        {
            var Q0;
            Q0=makeQuery(id+"F41.imprint","IMPRINT",FACE,{"disambiguationData":[TD([[makeQuery(id+"F41.imprint","IMPRINT",EDGE,{"derivedFrom":sQuery(id+"F41.wireOp",EDGE,"E114.0")}),1.0]])]});
            extrude(context, id + "F42", {"entities" : qUnion([Q0]), "operationType" : NewBodyOperationType.ADD, "depth" : 0.75 * mm});
        }
        {
            var Q0;
            Q0=makeQuery(id+"F40.boolean.opBoolean","COPY",FACE,{"derivedFrom":makeQuery(id+"F40.opExtrude","CAP_FACE",FACE,{"disambiguationData":[OSD([sQuery(id+"F39.wireOp",EDGE,"E112.0"),sQuery(id+"F39.wireOp",EDGE,"E113")])],"isStart":false})});
            var sketch = newSketch(context, id + "F43", { "sketchPlane" : qUnion([Q0])});
            skCircle(sketch, "E116.0", {"center": v(0, 30) * mm, "radius": 3.3 * mm});
            skCircle(sketch, "E117", {"center": v(0, 30) * mm, "radius": 5 * mm});
            skSolve(sketch);
        }
        {
            var Q0;
            Q0 = qSketchRegion(id + "F43", true);
            extrude(context, id + "F44", {"entities" : qUnion([Q0]), "operationType" : NewBodyOperationType.ADD, "depth" : 0.25 * mm});
        }
        {
            var Q0;
            Q0=makeQuery(id+"F42.opExtrude","CAP_FACE",FACE,{"disambiguationData":[OSD([sQuery(id+"F41.wireOp",EDGE,"E114.0"),sQuery(id+"F41.wireOp",EDGE,"E115")])],"isStart":false});
            var sketch = newSketch(context, id + "F45", { "sketchPlane" : qUnion([Q0])});
            skCircle(sketch, "E118.0", {"center": v(0, 30) * mm, "radius": 3.3 * mm});
            skCircle(sketch, "E119", {"center": v(0, 30) * mm, "radius": 5 * mm});
            skSolve(sketch);
        }
        {
            var Q0;
            Q0=makeQuery(id+"F45.imprint","IMPRINT",FACE,{"disambiguationData":[TD([[makeQuery(id+"F45.imprint","IMPRINT",EDGE,{"derivedFrom":sQuery(id+"F45.wireOp",EDGE,"E118.0")}),1.0]])]});
            extrude(context, id + "F46", {"entities" : qUnion([Q0]), "operationType" : NewBodyOperationType.ADD, "depth" : 0.25 * mm});
        }
        {
            var Q0;
            Q0=makeQuery(id+"F11.opExtrude","CAP_FACE",FACE,{"disambiguationData":[OSD([sQuery(id+"F10.wireOp",EDGE,"E52.0"),sQuery(id+"F10.wireOp",EDGE,"E53.0"),sQuery(id+"F10.wireOp",EDGE,"E54.0"),sQuery(id+"F10.wireOp",EDGE,"E55")])],"isStart":false});
            var sketch = newSketch(context, id + "F47", { "sketchPlane" : qUnion([Q0])});
            skPoint(sketch, "E120", {"position": v(35, -0.54) * mm});
            skPoint(sketch, "E121.MirrorP", {"position": v(-35, -0.54) * mm});
            skSolve(sketch);
        }
        {
            var Q0;
            Q0=sQuery(id+"F47.wireOp",VERTEX,"E121.MirrorP");
            var Q1;
            Q1=sQuery(id+"F47.wireOp",VERTEX,"E120");
            var Q2;
            Q2=makeQuery(id+"F1.opExtrude","SWEPT_BODY",BODY,{"disambiguationData":[OSD([sQuery(id+"F0.wireOp",EDGE,"7c40d91c-51bf-44e0-baa0-2f148f85da3b.MirrorCS"),sQuery(id+"F0.wireOp",EDGE,"E0.MirrorCS"),sQuery(id+"F0.wireOp",EDGE,"E1.MirrorCS"),sQuery(id+"F0.wireOp",EDGE,"E2.MirrorCS"),sQuery(id+"F0.wireOp",EDGE,"E3"),sQuery(id+"F0.wireOp",EDGE,"E4"),sQuery(id+"F0.wireOp",EDGE,"E5"),sQuery(id+"F0.wireOp",EDGE,"E6.MirrorCS"),sQuery(id+"F0.wireOp",EDGE,"E7.MirrorCS"),sQuery(id+"F0.wireOp",EDGE,"E8.MirrorCS"),sQuery(id+"F0.wireOp",EDGE,"2a2e974d-f992-448b-8597-4e99c86357490.MirrorCS"),sQuery(id+"F0.wireOp",EDGE,"E9.MirrorCS"),sQuery(id+"F0.wireOp",EDGE,"E10"),sQuery(id+"F0.wireOp",EDGE,"E11")])]});
            hole(context, id + "F48", {"style" : HoleStyle.SIMPLE, "endStyle" : HoleEndStyle.BLIND, "standardTappedOrClearance" : lookupTablePath({ "standard" : "ISO", "engagement" : "75%", "pitch" : "0.6 mm", "size" : "M3", "type" : "Tapped" }), "standardBlindInLast" : lookupTablePath({ "standard" : "ISO", "engagement" : "75%", "pitch" : "0.6 mm", "size" : "M3", "type" : "Tapped" }), "holeDiameter" : 2.4 * mm, "holeDepth" : 2.5 * mm, "locations" : qUnion([Q0, Q1]), "scope" : qUnion([Q2]), "startStyle" : HoleStartStyle.SKETCH});
        }
    });
